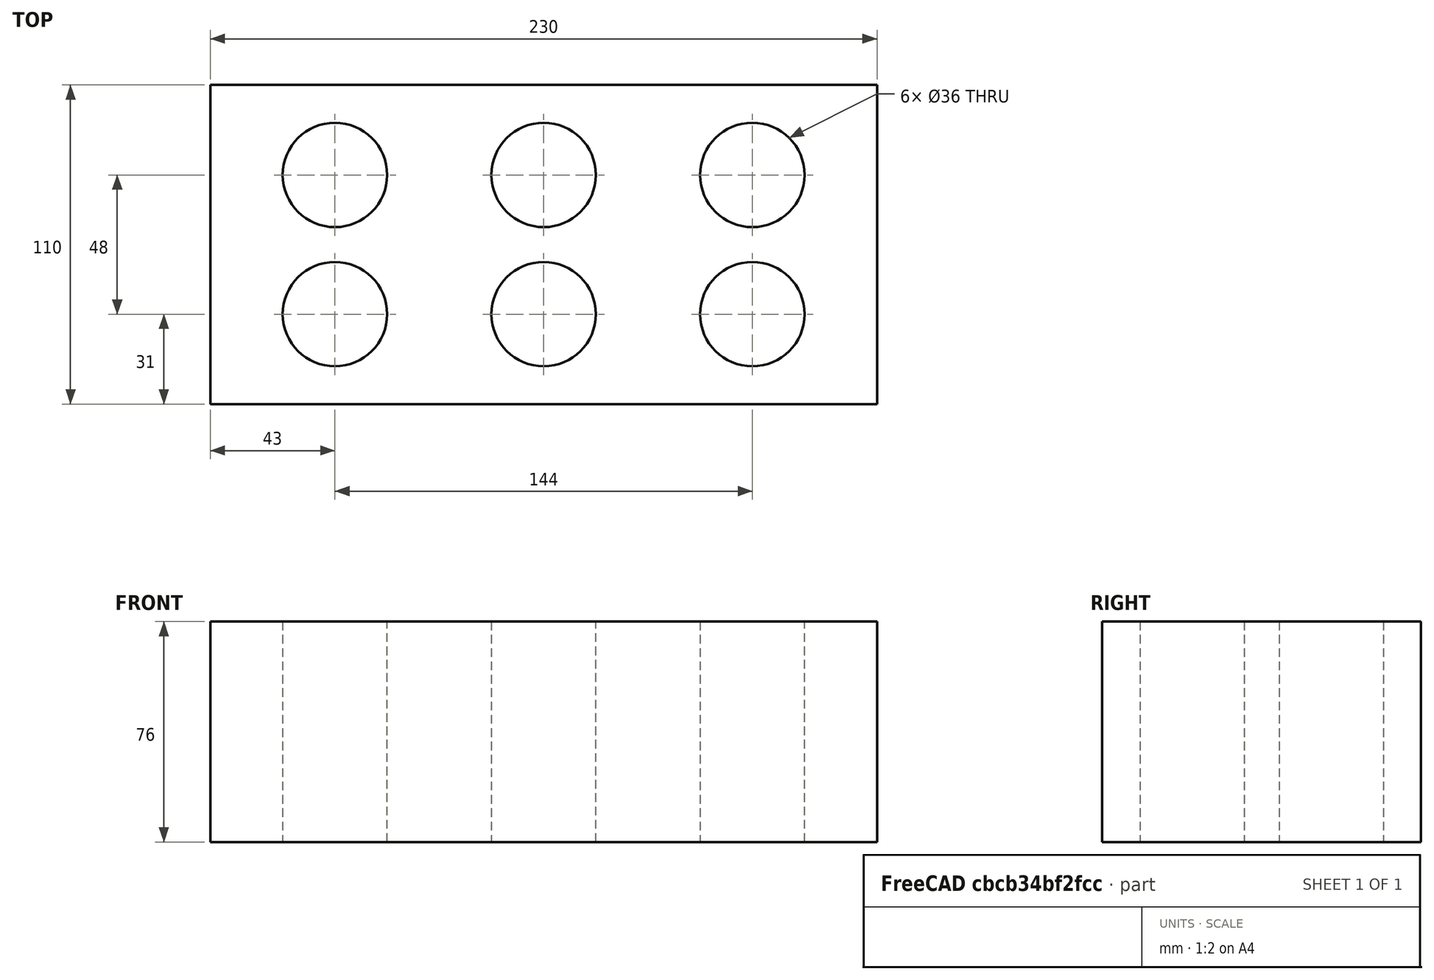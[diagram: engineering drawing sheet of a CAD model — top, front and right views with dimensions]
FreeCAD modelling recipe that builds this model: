
FCSTD DOCUMENT  (FreeCAD 1.0R39319 (Git))
Label: ojt1_t09_r02_brick
License: All rights reserved
LicenseURL: https://en.wikipedia.org/wiki/All_rights_reserved
objects: Part::Cylinder×6, Part::MultiFuse×3, Part::Cut×3, Part::Box×1
note: 13 computed .brp shape members not serialized (recipe doc carries the construction recipe); baked Part::Feature solids carry a one-line shape summary decoded from their .brp

FEATURE [Part::Box] Box  label="Cubo"
  AttacherType = Attacher::AttachEngine3D
  Height = 76
  Length = 230
  Width = 110
FEATURE [Part::Cylinder] Cylinder  label="Cilindro"
  Angle = 360
  AttacherType = Attacher::AttachEngine3D
  FirstAngle = 0
  Height = 76
  Placement = pos=(43,31,0) rot=(0,0,1;0rad)
  Radius = 18
  SecondAngle = 0
FEATURE [Part::Cylinder] Cylinder001  label="Cilindro001"
  Angle = 360
  AttacherType = Attacher::AttachEngine3D
  FirstAngle = 0
  Height = 76
  Placement = pos=(43,79,0) rot=(0,0,1;0rad)
  Radius = 18
  SecondAngle = 0
FEATURE [Part::MultiFuse] Fusion
  Refine = true
  Shapes = -> [Cylinder001,Cylinder]
FEATURE [Part::Cylinder] Cylinder002  label="Cilindro002"
  Angle = 360
  AttacherType = Attacher::AttachEngine3D
  FirstAngle = 0
  Height = 76
  Placement = pos=(43,31,0) rot=(0,0,1;0rad)
  Radius = 18
  SecondAngle = 0
FEATURE [Part::Cylinder] Cylinder003  label="Cilindro003"
  Angle = 360
  AttacherType = Attacher::AttachEngine3D
  FirstAngle = 0
  Height = 76
  Placement = pos=(43,79,0) rot=(0,0,1;0rad)
  Radius = 18
  SecondAngle = 0
FEATURE [Part::MultiFuse] Fusion001
  Placement = pos=(72,0,0) rot=(0,0,1;0rad)
  Refine = true
  Shapes = -> [Cylinder003,Cylinder002]
FEATURE [Part::Cylinder] Cylinder004  label="Cilindro004"
  Angle = 360
  AttacherType = Attacher::AttachEngine3D
  FirstAngle = 0
  Height = 76
  Placement = pos=(43,31,0) rot=(0,0,1;0rad)
  Radius = 18
  SecondAngle = 0
FEATURE [Part::Cylinder] Cylinder005  label="Cilindro005"
  Angle = 360
  AttacherType = Attacher::AttachEngine3D
  FirstAngle = 0
  Height = 76
  Placement = pos=(43,79,0) rot=(0,0,1;0rad)
  Radius = 18
  SecondAngle = 0
FEATURE [Part::MultiFuse] Fusion002
  Placement = pos=(144,0,0) rot=(0,0,1;0rad)
  Refine = true
  Shapes = -> [Cylinder005,Cylinder004]
FEATURE [Part::Cut] Cut
  Base = -> Box
  Refine = true
  Tool = -> Fusion
FEATURE [Part::Cut] Cut001
  Base = -> Cut
  Refine = true
  Tool = -> Fusion002
FEATURE [Part::Cut] Cut002
  Base = -> Cut001
  Refine = true
  Tool = -> Fusion001
